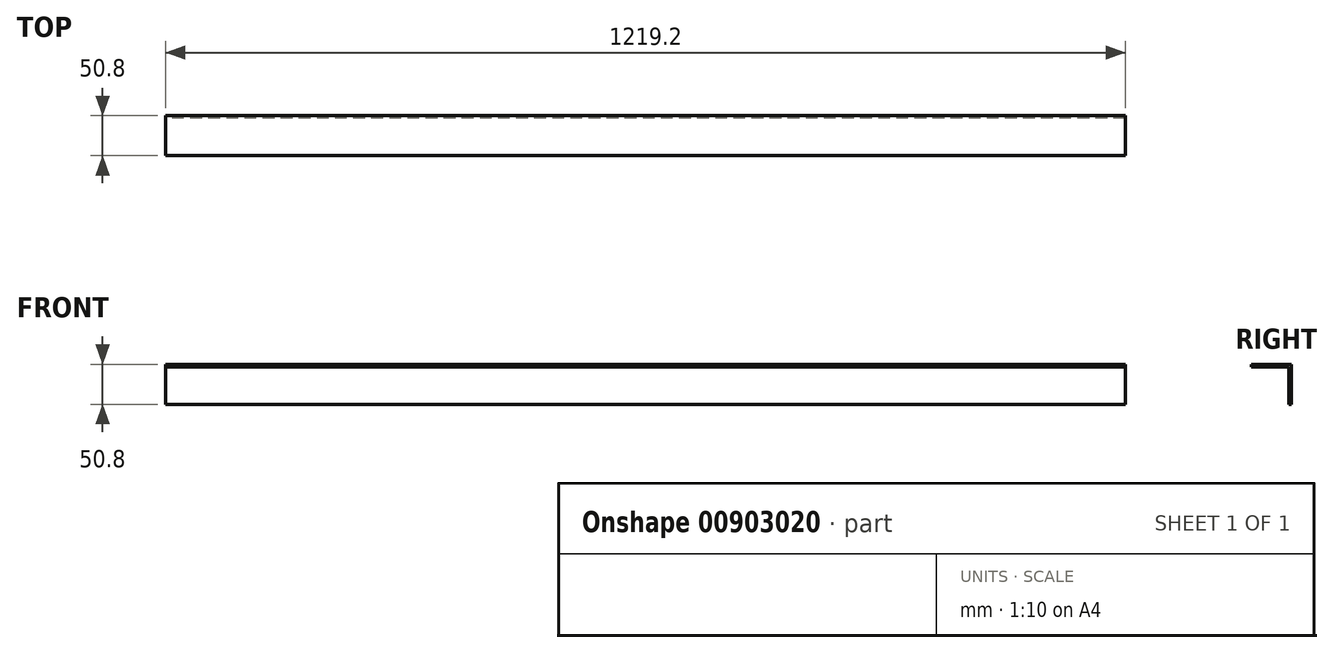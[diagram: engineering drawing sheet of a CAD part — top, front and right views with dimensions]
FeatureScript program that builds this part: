
annotation { "Feature Type Name" : "Feature", "Feature Type Description" : "" }
export const myFeature = defineFeature(function(context is Context, id is Id, definition is map)
    precondition{}
    {
        {
            var Q0;
            Q0=qCreatedBy(makeId("Right.planeOp"),FACE);
            var sketch = newSketch(context, id + "F0", { "sketchPlane" : qUnion([Q0])});
            skLineSegment(sketch, "E0", {"start": v(0, 0) * mm, "end": v(0, 50.8) * mm});
            skLineSegment(sketch, "E1", {"start": v(0, 50.8) * mm, "end": v(-50.8, 50.8) * mm});
            skLineSegment(sketch, "E2", {"start": v(-50.8, 50.8) * mm, "end": v(-50.8, 47.62) * mm});
            skLineSegment(sketch, "E3", {"start": v(-50.8, 47.62) * mm, "end": v(-3.18, 47.63) * mm});
            skLineSegment(sketch, "E4", {"start": v(-3.18, 47.63) * mm, "end": v(-3.17, 0) * mm});
            skLineSegment(sketch, "E5", {"start": v(-3.17, 0) * mm, "end": v(0, 0) * mm});
            skSolve(sketch);
        }
        {
            var Q0;
            Q0=makeQuery(id+"F0.imprint","IMPRINT",FACE,{"disambiguationData":[TD([[makeQuery(id+"F0.imprint","IMPRINT",EDGE,{"derivedFrom":sQuery(id+"F0.wireOp",EDGE,"E0")}),1.0]])]});
            extrude(context, id + "F1", {"entities" : qUnion([Q0]), "depth" : 1219.2 * mm, "offsetDistance" : 25.4 * mm});
        }
    });
